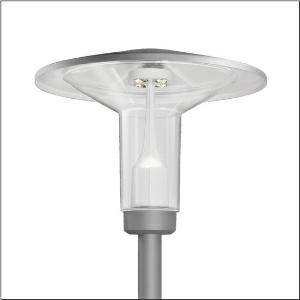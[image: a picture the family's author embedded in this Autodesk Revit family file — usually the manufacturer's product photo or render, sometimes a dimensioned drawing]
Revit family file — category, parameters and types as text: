
# Revit family: laterne_iq___p1_0a_5xa5255nf14h_4412
name_source: partatom
category: Lighting Fixtures
units: mm (PartAtom-declared; Revit-internal decimal feet)

## family parameters
Cut with Voids When Loaded = No
Host = Face
Light Source = No
Part Type = Normal
Room Calculation Point = No
Round Connector Dimension = Use Diameter
Shared = No

## types (1)
- --- (1 x LED, 1510 lm, 11.8 W, 2700K)
    Apparent Load = 12 VA
    CIE Flux Codes = 35 64 91 96 100
    Color Rendering = 70
    Color Temperature = 2700K
    Default Elevation = 1800 mm
    Description = Lantern iQ, mast luminaire, Module 540 iQ-SR, primary light control with 3 zone facetted reflector, of plastic, silver coated, highly specular, structured, primary optical cover: cover, of PMMA, transparent, light distribution: P1.0a, light emission: direct distribution, primary light characteristic: strongly asymmetric, installation type: post-top, LED, High Power LED, rated luminous flux: 1.510lm, luminous efficacy: 128lm/W, light colour: 727, colour temperature: 2700K, control gear: iQ Street-Remote, control: pre-setting: logarithmic dimming characteristic, Street-Remote, Auto-Match, Temp-Guard, Lumen-Switch, Night-Set, Smart-Wire, Light-Fading, Desk-Remote (wireless, voltage-free reading and setting of iQ features in the workshop via application-optimized NFC function/RFID function), optimised constant luminous flux control (CLO 2.0), with terminal, 6-pole, max. 2.5mm², mains connection: 230..240V, AC, 50/60Hz, start of lifetime: 12W, end of service life: 12W, reduction: 6W, luminaire housing, upper part, of glass-fibre reinforced polyester, coated, Siteco® metallic grey (DB 702S), diameter: 750mm, height: 583mm, spigot size: d x l = 76 x 70mm (post-top) | with reducer (optional accessory) 60 x 70mm, mounting height: 3..5m, post-top mast mounting element, of diecast aluminium, coated, Siteco® metallic grey (DB 702S), Module 540 iQ-SR, traffic white (RAL 9016), equipment: standard, protection rating (complete): IP65, insulation class (complete): insulation class II (safety insulation), certification: CE, ENEC, VDE, packaging unit: 1 piece

Light Distribution: P1.0a
    Height = 583 mm
    Lamp = 1 x LED
    Lamp Light Flux = 1510 lm
    Lamp Power = 11.8 W
    Lamp count = 1
    Length = 750 mm
    Luminous efficacy = 128 lm/W
    Manufacturer = Siteco
    ModVariant = No
    Model = 5XA5255NF14H
    Mounting Place = Pole
    Mounting Type = Pole top
    Number of Poles = 1
    OnlyDefault = Yes
    Power Factor = 1
    Product Name = Laterne iQ | P1.0a
    Product group = mast luminaire | pylon top
    ProductGroupID = 6100
    Protection Class = Protection class II
    Protection Degree = IP 65
    RLX_Detail_Level = 1
    RLX_Emergency_Light_Flux = 0 lm
    RLX_Emergency_Type = 0
    RLX_Emergency_Type_DB = No
    RlxData = <blob elided: 73897 chars, md5=3764eb18>
    Socket = socket
    Standby Power = 0 W
    System Light Flux = 1510 lm
    System Power = 12 W
    Type Comments = factory setting: luminous flux: 100 % | dim-lin: 254 | 472 mA
    Type Image = l_1006050.jpg
    URL = http://relux.com
    VarID = @adj_154423
    Voltage = 0 V
    Weight = 0.00 kg
    Width = 0 mm  [stored 0 ft]

note: [stored X ft] marks values corroborated as IEEE doubles in the binary element streams (Revit-internal decimal feet)

## geometry (parser evidence)
native form markers: Blend x4, Sweep x11
no freeform markers — native parametric forms only
